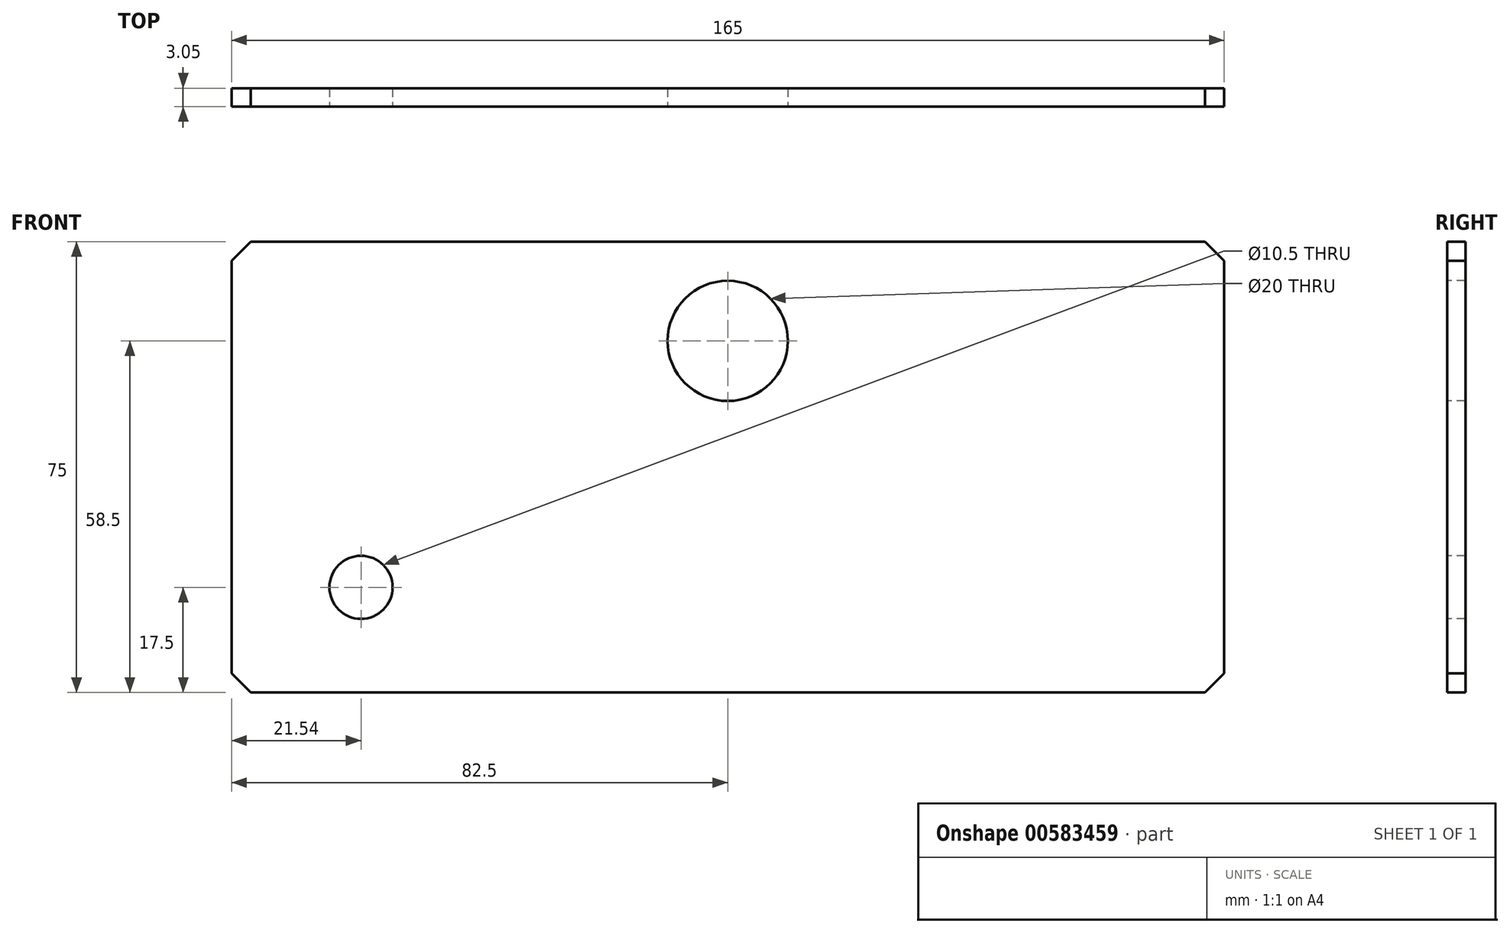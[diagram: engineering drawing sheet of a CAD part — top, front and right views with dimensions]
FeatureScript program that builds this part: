
annotation { "Feature Type Name" : "Feature", "Feature Type Description" : "" }
export const myFeature = defineFeature(function(context is Context, id is Id, definition is map)
    precondition{}
    {
        {
            var Q0;
            Q0=qCreatedBy(makeId("Front.planeOp"),FACE);
            var sketch = newSketch(context, id + "F0", { "sketchPlane" : qUnion([Q0])});
            skLineSegment(sketch, "E0.bottom", {"start": v(82.5, 0) * mm, "end": v(-82.5, 0) * mm});
            skLineSegment(sketch, "E0.top", {"start": v(82.5, 75) * mm, "end": v(-82.5, 75) * mm});
            skLineSegment(sketch, "E0.left", {"start": v(82.5, 0) * mm, "end": v(82.5, 75) * mm});
            skLineSegment(sketch, "E0.right", {"start": v(-82.5, 0) * mm, "end": v(-82.5, 75) * mm});
            skPoint(sketch, "E0.middle", {"position": v(0, 0) * mm});
            skSolve(sketch);
        }
        {
            var Q0;
            Q0=qSketchRegion(id+"F0",true);
            extrude(context, id + "F1", {"entities" : qUnion([Q0]), "depth" : 3.05 * mm, "offsetDistance" : 25.4 * mm});
        }
        {
            var Q0;
            Q0=makeQuery(id+"F1.opExtrude","CAP_FACE",FACE,{"disambiguationData":[OSD([sQuery(id+"F0.wireOp",EDGE,"E0.bottom"),sQuery(id+"F0.wireOp",EDGE,"E0.top"),sQuery(id+"F0.wireOp",EDGE,"E0.left"),sQuery(id+"F0.wireOp",EDGE,"E0.right")])],"isStart":false});
            var sketch = newSketch(context, id + "F2", { "sketchPlane" : qUnion([Q0])});
            skCircle(sketch, "E1", {"center": v(-60.96, 17.5) * mm, "radius": 5.25 * mm});
            skSolve(sketch);
        }
        {
            var Q0;
            Q0=qSketchRegion(id+"F2",true);
            extrude(context, id + "F3", {"entities" : qUnion([Q0]), "operationType" : NewBodyOperationType.REMOVE, "oppositeDirection" : true, "depth" : 3.05 * mm, "offsetDistance" : 25.4 * mm});
        }
        {
            var Q0;
            Q0=makeQuery(id+"F1.opExtrude","CAP_FACE",FACE,{"disambiguationData":[OSD([sQuery(id+"F0.wireOp",EDGE,"E0.bottom"),sQuery(id+"F0.wireOp",EDGE,"E0.top"),sQuery(id+"F0.wireOp",EDGE,"E0.left"),sQuery(id+"F0.wireOp",EDGE,"E0.right")])],"isStart":false});
            var sketch = newSketch(context, id + "F4", { "sketchPlane" : qUnion([Q0])});
            skCircle(sketch, "E2", {"center": v(0, 58.5) * mm, "radius": 10 * mm});
            skSolve(sketch);
        }
        {
            var Q0;
            Q0 = qSketchRegion(id + "F4", true);
            extrude(context, id + "F5", {"entities" : qUnion([Q0]), "operationType" : NewBodyOperationType.REMOVE, "oppositeDirection" : true, "depth" : 3.05 * mm, "offsetDistance" : 25.4 * mm});
        }
        {
            var Q0;
            Q0=makeQuery(id+"F1.opExtrude","SWEPT_EDGE",EDGE,{"disambiguationData":[OSD([sQuery(id+"F0.wireOp",EDGE,"E0.top"),sQuery(id+"F0.wireOp",EDGE,"E0.right")])]});
            var Q1;
            Q1=makeQuery(id+"F1.opExtrude","SWEPT_EDGE",EDGE,{"disambiguationData":[OSD([sQuery(id+"F0.wireOp",EDGE,"E0.bottom"),sQuery(id+"F0.wireOp",EDGE,"E0.right")])]});
            var Q2;
            Q2=makeQuery(id+"F1.opExtrude","SWEPT_EDGE",EDGE,{"disambiguationData":[OSD([sQuery(id+"F0.wireOp",EDGE,"E0.bottom"),sQuery(id+"F0.wireOp",EDGE,"E0.left")])]});
            var Q3;
            Q3=makeQuery(id+"F1.opExtrude","SWEPT_EDGE",EDGE,{"disambiguationData":[OSD([sQuery(id+"F0.wireOp",EDGE,"E0.top"),sQuery(id+"F0.wireOp",EDGE,"E0.left")])]});
            chamfer(context, id + "F6", {"entities" : qUnion([Q0, Q1, Q2, Q3]), "width" : 3.17 * mm, "tangentPropagation" : true});
        }
    });
